# Revit family: WashBasin-50cm-Vitra-MetropolSeries_5661B003-0001
name_source: partatom
category: Plumbing Fixtures
revit_build: Autodesk Revit 2017 (Build: 20160225_1515(x64)
units: mm (PartAtom-declared; Revit-internal decimal feet)

## family parameters
Cut with Voids When Loaded = No
Host = Face
OmniClass Number = 23.45.05.14.14
OmniClass Title = Sinks/Lavatories
Part Type = Normal
Room Calculation Point = No
Round Connector Dimension = Use Diameter
Shared = Yes

## types (4) — shared parameters
BIMobject category = Sanitary - Basins
Brand = VitrA
CW Connection = No
Color = White
Default Elevation = 850 mm  [stored 2.78871 ft]
Design country = Turkey
HW Connection = No
IFC Classification = Sanitary Terminal
Main Material = Ceramic
Manufacturer = Vitra
Manufacturer name = Vitra
Masterformat 2014 Code = 22 41 16
Masterformat 2014 Description = Residential Lavatories and Sinks
MountingType = Wall Mounted
NBS Referans Code = 35-65-70-94
NBS Referans Description = Wash Basin Systems
Nominal Depth = 460 mm  [stored 1.50919 ft]
NominalHeight = 170 mm  [stored 0.557743 ft]
NominalWidth = 505 mm
OmniClass Code = 23.45.05.14.14
OmniClass Description = Sinks/Lavatories
Product certification = https://www.vitraglobal.com
Product data url = https://www.vitraglobal.com
Product family = Wall Mounted WashBasin
Product group = Metropol
Secondary Material = Ceramic-White
Technical description = https://www.vitraglobal.com
UNSPSC Code = 301815
URL = https://vitraglobal.com
Uniclass 1.4 Code = L7212
Uniclass 1.4 Description = Washbasins
Uniclass 2.0 Code = SS-35-65-70-94
Uniclass 2.0 Description = Sanitary Dispensing And Disposal Units
Uniclass 2015 Code = Pr_40_20_96_81
Uniclass 2015 Name = Wash basins, Sinks and troughs
Uniformat II Code = D2010
Uniformat II Description = Plumbing Fixtures
Vent Connection = No
Warranty Period (Year) = 10 Years
Waste Connection = Yes
Weight Net (kg) = 13,1
Youtube = https://www.youtube.com
zero-valued in all types: Cost

## per-type parameters (varying)
| type | Article No. (default) | Description | Hole | Model | Product SKU |
| WashBasin-50cm-Vitra-MetropolSeries_5661B003-0001 | 5661B003-0001 | VitrA Metropol - With Tap Hole, With Overflow Hole, 50 cm, | Yes | 5661B003-0001 | 5661B003-0001 |
| WashBasin-50cm-Vitra-MetropolSeries_5661B003-0041 | 5661B003-0041 | VitrA Metropol - With Tap Hole, Without Overflow Hole, 50 cm | No | 5661B003-0041 | 5661B003-0041 |
| WashBasin-50cm-Vitra-MetropolSeries_5661B003-0937 | 5661B003-0937 | VitrA Metropol - With Tap Hole, Without Overflow Hole, 50 cm | No | 5661B003-0937 | 5661B003-0937 |
| WashBasin-50cm-Vitra-MetropolSeries_5661B003-0973 | 5661B003-0973 | VitrA Metropol - With Tap Hole, With Overflow Hole, 50 cm, | Yes | 5661B003-0973 | 5661B003-0973 |

note: [stored X ft] marks values corroborated as IEEE doubles in the binary element streams (Revit-internal decimal feet)

## geometry (parser evidence)
native form markers: Sweep x3
no freeform markers — native parametric forms only
